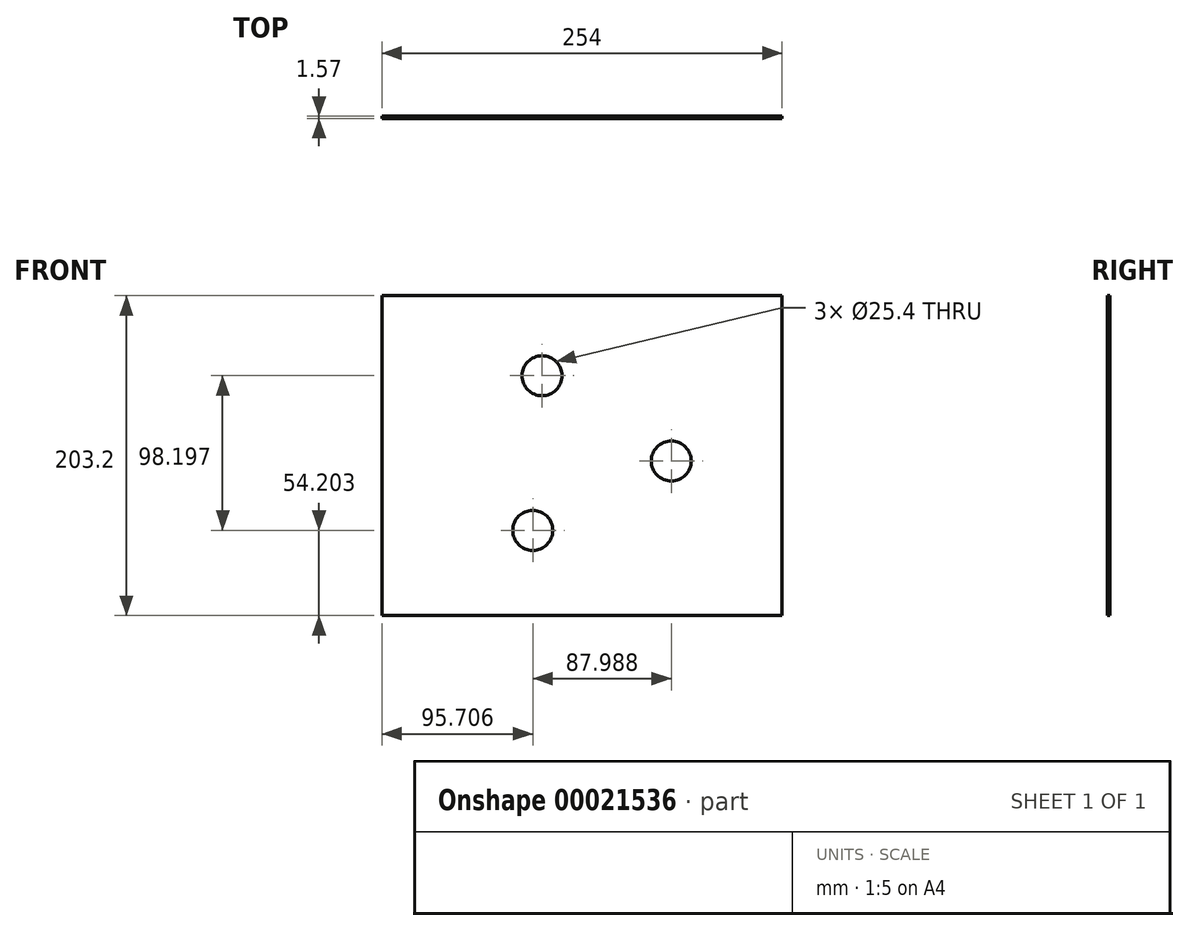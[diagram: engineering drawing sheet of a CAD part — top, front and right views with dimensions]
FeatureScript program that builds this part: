
annotation { "Feature Type Name" : "Feature", "Feature Type Description" : "" }
export const myFeature = defineFeature(function(context is Context, id is Id, definition is map)
    precondition{}
    {
        {
            var Q0;
            Q0=qCreatedBy(makeId("Front.planeOp"),FACE);
            var sketch = newSketch(context, id + "F0", { "sketchPlane" : qUnion([Q0])});
            skLineSegment(sketch, "E0.rect.bottom", {"start": v(127, 101.6) * mm, "end": v(-127, 101.6) * mm});
            skLineSegment(sketch, "E0.rect.top", {"start": v(127, -101.6) * mm, "end": v(-127, -101.6) * mm});
            skLineSegment(sketch, "E0.rect.left", {"start": v(127, 101.6) * mm, "end": v(127, -101.6) * mm});
            skLineSegment(sketch, "E0.rect.right", {"start": v(-127, 101.6) * mm, "end": v(-127, -101.6) * mm});
            skPoint(sketch, "E0.rect.middle", {"position": v(0, 0) * mm});
            skCircle(sketch, "E1", {"center": v(-25.4, 50.8) * mm, "radius": 12.7 * mm});
            skCircle(sketch, "E2.1.0", {"center": v(-31.3, -47.4) * mm, "radius": 12.7 * mm});
            skCircle(sketch, "E2.2.0", {"center": v(56.7, -3.4) * mm, "radius": 12.7 * mm});
            skSolve(sketch);
        }
        {
            var Q0;
            Q0=makeQuery(id+"F0.imprint","IMPRINT",FACE,{"disambiguationData":[TD([[makeQuery(id+"F0.imprint","IMPRINT",EDGE,{"derivedFrom":sQuery(id+"F0.wireOp",EDGE,"E0.rect.bottom")}),1.0]])]});
            extrude(context, id + "F1", {"entities" : qUnion([Q0]), "depth" : 1.57 * mm});
        }
    });
